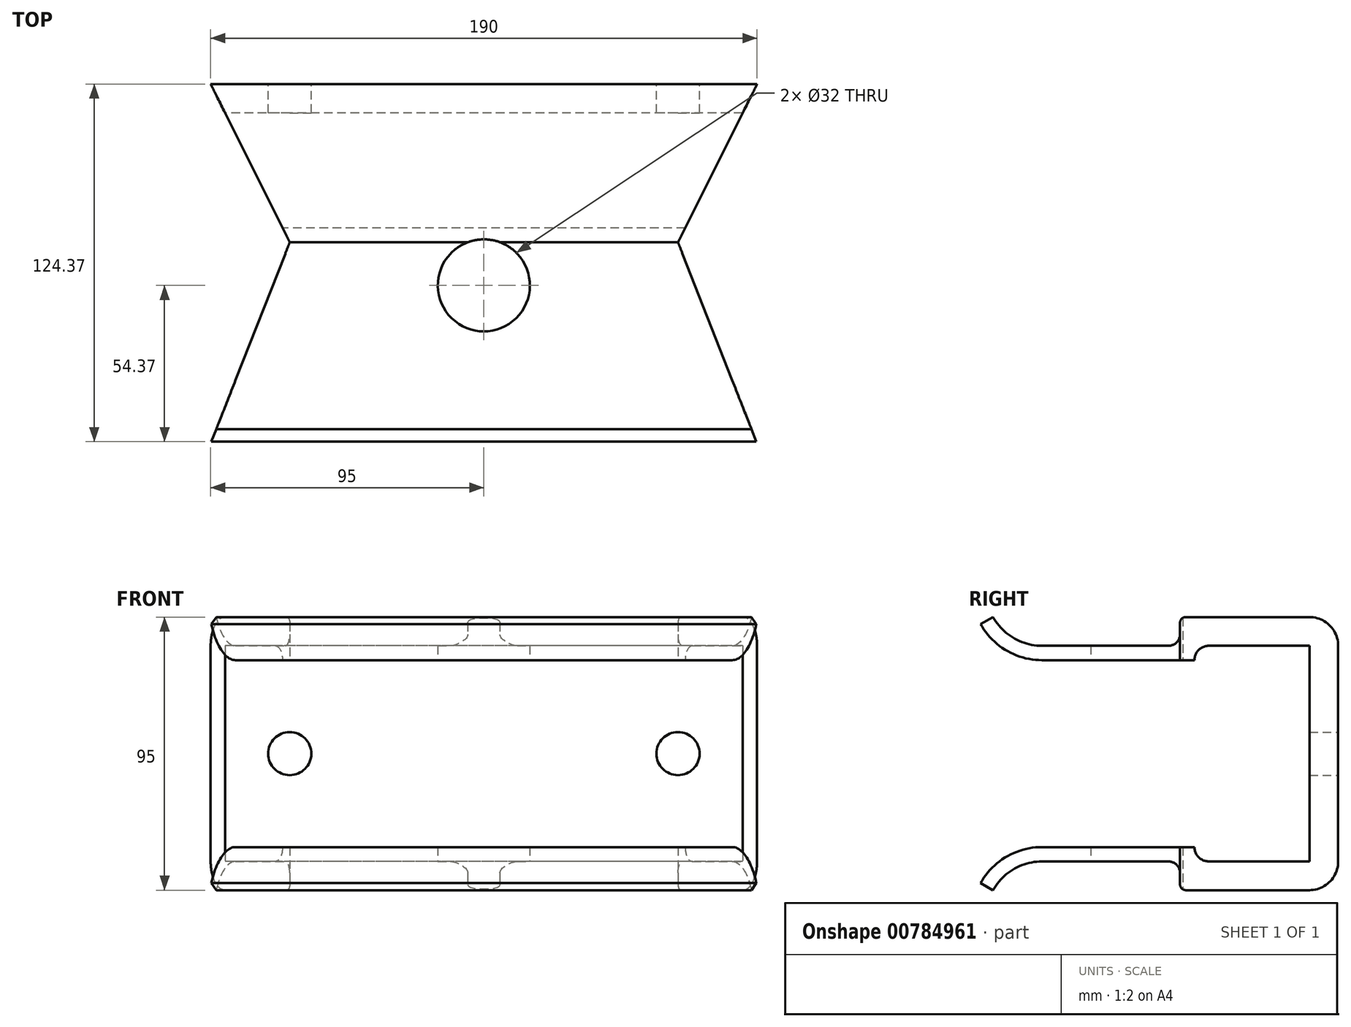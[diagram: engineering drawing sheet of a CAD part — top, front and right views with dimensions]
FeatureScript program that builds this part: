
annotation { "Feature Type Name" : "Feature", "Feature Type Description" : "" }
export const myFeature = defineFeature(function(context is Context, id is Id, definition is map)
    precondition{}
    {
        {
            var Q0;
            Q0=qCreatedBy(makeId("Top.planeOp"),FACE);
            var sketch = newSketch(context, id + "F0", { "sketchPlane" : qUnion([Q0])});
            skLineSegment(sketch, "E0", {"start": v(0, 0) * mm, "end": v(95, 0) * mm});
            skLineSegment(sketch, "E1", {"start": v(95, 0) * mm, "end": v(67.5, -55) * mm});
            skLineSegment(sketch, "E2", {"start": v(67.5, -55) * mm, "end": v(95, -125) * mm});
            skLineSegment(sketch, "E3", {"start": v(95, -125) * mm, "end": v(0, -125) * mm});
            skLineSegment(sketch, "E4.MirrorCS", {"start": v(-95, 0) * mm, "end": v(-67.5, -55) * mm});
            skLineSegment(sketch, "E5.MirrorCS", {"start": v(0, 0) * mm, "end": v(-95, 0) * mm});
            skLineSegment(sketch, "E6.MirrorCS", {"start": v(-67.5, -55) * mm, "end": v(-95, -125) * mm});
            skLineSegment(sketch, "E7.MirrorCS", {"start": v(-95, -125) * mm, "end": v(0, -125) * mm});
            skCircle(sketch, "E8", {"center": v(0, -70) * mm, "radius": 16 * mm});
            skSolve(sketch);
        }
        {
            var Q0;
            Q0=makeQuery(id+"F0.imprint","IMPRINT",FACE,{"disambiguationData":[TD([[makeQuery(id+"F0.imprint","IMPRINT",EDGE,{"derivedFrom":sQuery(id+"F0.wireOp",EDGE,"E0")}),-1.0]])]});
            extrude(context, id + "F1", {"entities" : qUnion([Q0]), "endBound" : BoundingType.SYMMETRIC, "depth" : 95 * mm, "offsetDistance" : 25 * mm});
        }
        {
            var Q0;
            Q0=qCreatedBy(makeId("Right.planeOp"),FACE);
            var sketch = newSketch(context, id + "F2", { "sketchPlane" : qUnion([Q0])});
            skLineSegment(sketch, "E9", {"start": v(0, 0) * mm, "end": v(0, 37.5) * mm});
            skArc(sketch, "E10", {"start": v(0, 37.5) * mm, "mid": v(-2.93, 44.57) * mm, "end": v(-10, 47.5) * mm});
            skLineSegment(sketch, "E11", {"start": v(-10, 47.5) * mm, "end": v(-53, 47.5) * mm});
            skLineSegment(sketch, "E12", {"start": v(-55, 45.5) * mm, "end": v(-55, 41.5) * mm});
            skLineSegment(sketch, "E13", {"start": v(-59, 37.5) * mm, "end": v(-103, 37.5) * mm});
            skArc(sketch, "E14", {"start": v(-120, 47.5) * mm, "mid": v(-112.86, 40.19) * mm, "end": v(-103, 37.5) * mm});
            skPoint(sketch, "E15.visualSharp", {"position": v(-55, 37.5) * mm});
            skArc(sketch, "E15.filletArc", {"start": v(-59, 37.5) * mm, "mid": v(-56.17, 38.67) * mm, "end": v(-55, 41.5) * mm});
            skLineSegment(sketch, "E16.0", {"start": v(-10, 0) * mm, "end": v(-10, 37.5) * mm});
            skLineSegment(sketch, "E17.0", {"start": v(-10, 37.5) * mm, "end": v(-45, 37.5) * mm});
            skLineSegment(sketch, "E18.0", {"start": v(-103, 32.5) * mm, "end": v(-103, 32.5) * mm});
            skArc(sketch, "E18.1", {"start": v(-124.37, 45.07) * mm, "mid": v(-115.4, 35.88) * mm, "end": v(-103, 32.5) * mm});
            skPoint(sketch, "E19.visualSharp", {"position": v(-55, 47.5) * mm});
            skArc(sketch, "E19.filletArc", {"start": v(-53, 47.5) * mm, "mid": v(-54.41, 46.91) * mm, "end": v(-55, 45.5) * mm});
            skLineSegment(sketch, "E20", {"start": v(-103, 32.5) * mm, "end": v(-50, 32.5) * mm});
            skLineSegment(sketch, "E21", {"start": v(-50, 32.5) * mm, "end": v(-50, 32.5) * mm});
            skLineSegment(sketch, "E22", {"start": v(-10, 0) * mm, "end": v(0, 0) * mm});
            skLineSegment(sketch, "E23", {"start": v(-124.37, 45.07) * mm, "end": v(-120, 47.5) * mm});
            skPoint(sketch, "E24.visualSharp", {"position": v(-50, 37.5) * mm});
            skArc(sketch, "E24.filletArc", {"start": v(-45, 37.5) * mm, "mid": v(-48.54, 36.04) * mm, "end": v(-50, 32.5) * mm});
            skArc(sketch, "E25.MirrorCS", {"start": v(-53, -47.5) * mm, "mid": v(-54.41, -46.91) * mm, "end": v(-55, -45.5) * mm});
            skArc(sketch, "E26.MirrorCS", {"start": v(-59, -37.5) * mm, "mid": v(-56.17, -38.67) * mm, "end": v(-55, -41.5) * mm});
            skLineSegment(sketch, "E27.MirrorCS", {"start": v(-55, -45.5) * mm, "end": v(-55, -41.5) * mm});
            skLineSegment(sketch, "E28.MirrorCS", {"start": v(-124.37, -45.07) * mm, "end": v(-120, -47.5) * mm});
            skArc(sketch, "E29.MirrorCS", {"start": v(-45, -37.5) * mm, "mid": v(-48.54, -36.04) * mm, "end": v(-50, -32.5) * mm});
            skLineSegment(sketch, "E30.MirrorCS", {"start": v(-10, -37.5) * mm, "end": v(-45, -37.5) * mm});
            skArc(sketch, "E31.MirrorCS", {"start": v(-124.37, -45.07) * mm, "mid": v(-115.4, -35.88) * mm, "end": v(-103, -32.5) * mm});
            skPoint(sketch, "E32.MirrorP", {"position": v(-55, -37.5) * mm});
            skLineSegment(sketch, "E33.MirrorCS", {"start": v(0, 0) * mm, "end": v(0, -37.5) * mm});
            skArc(sketch, "E34.MirrorCS", {"start": v(0, -37.5) * mm, "mid": v(-2.93, -44.57) * mm, "end": v(-10, -47.5) * mm});
            skLineSegment(sketch, "E35.MirrorCS", {"start": v(-10, -47.5) * mm, "end": v(-53, -47.5) * mm});
            skLineSegment(sketch, "E36.MirrorCS", {"start": v(-103, -32.5) * mm, "end": v(-50, -32.5) * mm});
            skArc(sketch, "E37.MirrorCS", {"start": v(-120, -47.5) * mm, "mid": v(-112.86, -40.19) * mm, "end": v(-103, -37.5) * mm});
            skLineSegment(sketch, "E38.MirrorCS", {"start": v(-50, -32.5) * mm, "end": v(-50, -32.5) * mm});
            skLineSegment(sketch, "E39.MirrorCS", {"start": v(-59, -37.5) * mm, "end": v(-103, -37.5) * mm});
            skLineSegment(sketch, "E40.MirrorCS", {"start": v(-10, 0) * mm, "end": v(-10, -37.5) * mm});
            skPoint(sketch, "E41.MirrorP", {"position": v(-55, -47.5) * mm});
            skLineSegment(sketch, "E42.MirrorCS", {"start": v(-103, -32.5) * mm, "end": v(-103, -32.5) * mm});
            skPoint(sketch, "E43.MirrorP", {"position": v(-50, -37.5) * mm});
            skSolve(sketch);
        }
        {
            var Q0;
            Q0 = qSketchRegion(id + "F2", true);
            extrude(context, id + "F3", {"entities" : qUnion([Q0]), "operationType" : NewBodyOperationType.INTERSECT, "endBound" : BoundingType.SYMMETRIC, "depth" : 190 * mm, "offsetDistance" : 25 * mm});
        }
        {
            var Q0;
            Q0=makeQuery(id+"F1.opExtrude","SWEPT_FACE",FACE,{"disambiguationData":[OSD([sQuery(id+"F0.wireOp",EDGE,"E0"),sQuery(id+"F0.wireOp",EDGE,"E5.MirrorCS")])]});
            var sketch = newSketch(context, id + "F4", { "sketchPlane" : qUnion([Q0])});
            skPoint(sketch, "E44", {"position": v(67.5, 0) * mm});
            skPoint(sketch, "E45.MirrorP", {"position": v(-67.5, 0) * mm});
            skSolve(sketch);
        }
        {
            var Q0;
            Q0=sQuery(id+"F4.wireOp",VERTEX,"E44");
            var Q1;
            Q1=sQuery(id+"F4.wireOp",VERTEX,"E45.MirrorP");
            var Q2;
            Q2=makeQuery(id+"F1.opExtrude","SWEPT_BODY",BODY,{"disambiguationData":[OSD([sQuery(id+"F0.wireOp",EDGE,"E0"),sQuery(id+"F0.wireOp",EDGE,"E1"),sQuery(id+"F0.wireOp",EDGE,"E2"),sQuery(id+"F0.wireOp",EDGE,"E3"),sQuery(id+"F0.wireOp",EDGE,"E4.MirrorCS"),sQuery(id+"F0.wireOp",EDGE,"E5.MirrorCS"),sQuery(id+"F0.wireOp",EDGE,"E6.MirrorCS"),sQuery(id+"F0.wireOp",EDGE,"E7.MirrorCS"),sQuery(id+"F0.wireOp",EDGE,"E8")])]});
            hole(context, id + "F5", {"style" : HoleStyle.SIMPLE, "endStyle" : HoleEndStyle.THROUGH, "holeDiameter" : 15 * mm, "majorDiameter" : 5 * mm, "isTappedThrough" : true, "tappedDepth" : 12 * mm, "tapClearance" : 3, "locations" : qUnion([Q0, Q1]), "scope" : qUnion([Q2])});
        }
    });
